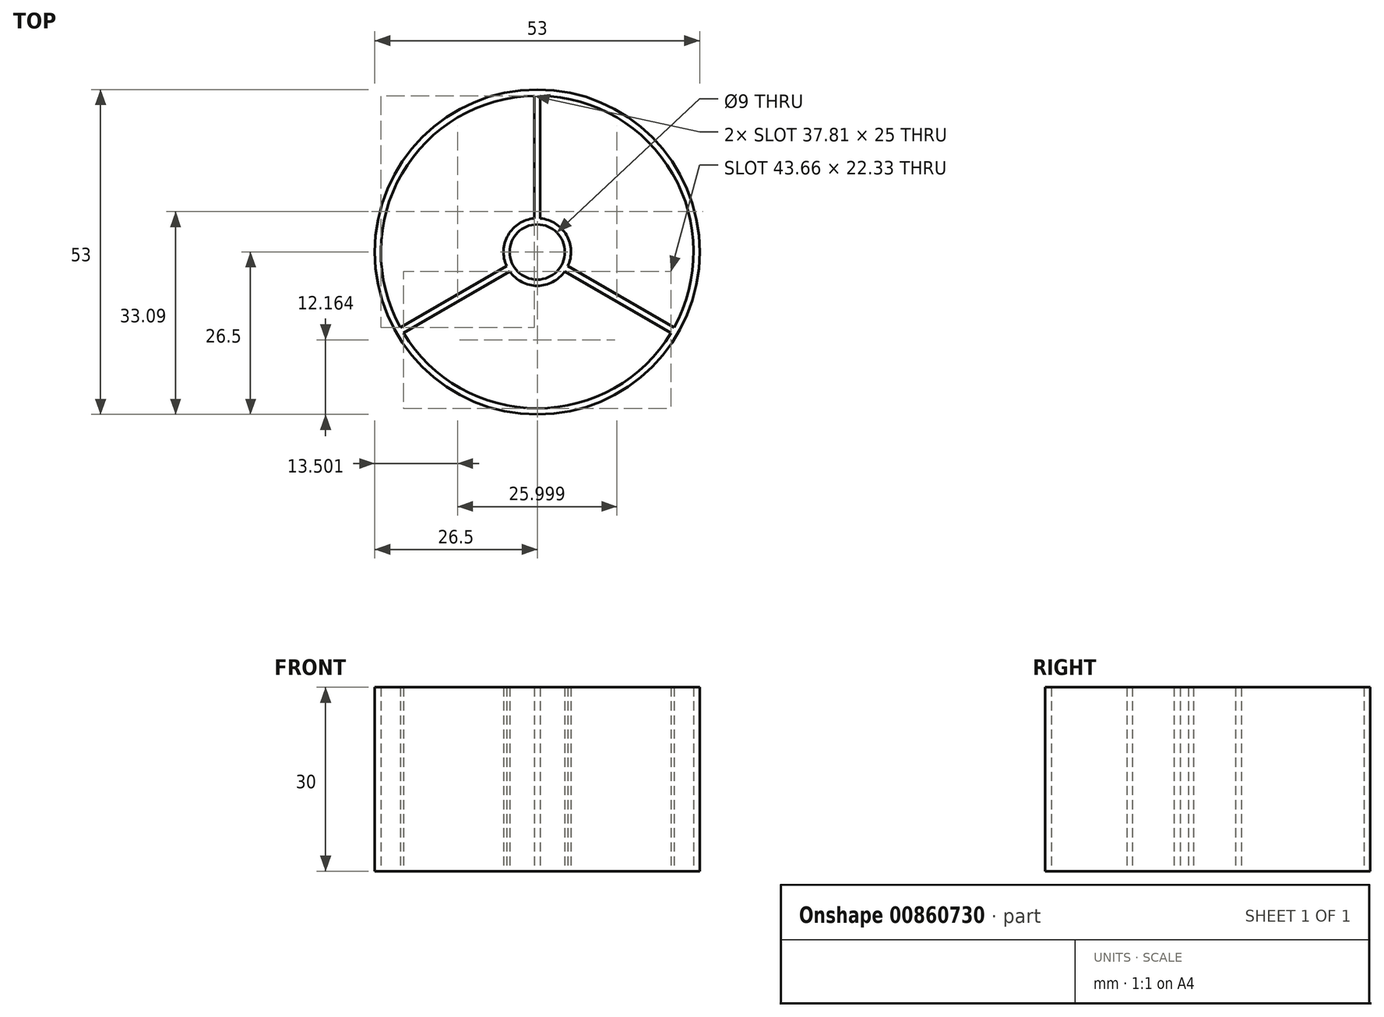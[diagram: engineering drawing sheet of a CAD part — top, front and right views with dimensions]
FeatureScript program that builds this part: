
annotation { "Feature Type Name" : "Feature", "Feature Type Description" : "" }
export const myFeature = defineFeature(function(context is Context, id is Id, definition is map)
    precondition{}
    {
        {
            var Q0;
            Q0=qCreatedBy(makeId("Top.planeOp"),FACE);
            var sketch = newSketch(context, id + "F0", { "sketchPlane" : qUnion([Q0])});
            skCircle(sketch, "E0", {"center": v(0, 0) * mm, "radius": 26.5 * mm});
            skCircle(sketch, "E1.0", {"center": v(0, 0) * mm, "radius": 25.5 * mm});
            skCircle(sketch, "E2", {"center": v(0, 0) * mm, "radius": 4.5 * mm});
            skCircle(sketch, "E3.0", {"center": v(0, 0) * mm, "radius": 5.5 * mm});
            skLineSegment(sketch, "E4", {"start": v(-0.5, 5.48) * mm, "end": v(-0.5, 25.5) * mm});
            skLineSegment(sketch, "E5", {"start": v(0.5, 5.48) * mm, "end": v(0.5, 25.5) * mm});
            skLineSegment(sketch, "E6.1.0", {"start": v(-4.5, -3.17) * mm, "end": v(-21.83, -13.18) * mm});
            skLineSegment(sketch, "E6.1.1", {"start": v(-5, -2.3) * mm, "end": v(-22.33, -12.31) * mm});
            skLineSegment(sketch, "E6.2.0", {"start": v(5, -2.3) * mm, "end": v(22.33, -12.31) * mm});
            skLineSegment(sketch, "E6.2.1", {"start": v(4.5, -3.17) * mm, "end": v(21.83, -13.18) * mm});
            skSolve(sketch);
        }
        {
            var Q0;
            Q0=makeQuery(id+"F0.imprint","IMPRINT",FACE,{"disambiguationData":[TD([[makeQuery(id+"F0.imprint","IMPRINT",EDGE,{"derivedFrom":sQuery(id+"F0.wireOp",EDGE,"E0")}),1.0]])]});
            var Q1;
            Q1=makeQuery(id+"F0.imprint","IMPRINT",FACE,{"disambiguationData":[TD([[makeQuery(id+"F0.imprint","IMPRINT",EDGE,{"derivedFrom":sQuery(id+"F0.wireOp",EDGE,"E2")}),-1.0]])]});
            var Q2;
            {var subQ0=sQuery(id+"F0.wireOp",EDGE,"E4");Q2=makeQuery(id+"F0.imprint","IMPRINT",FACE,{"disambiguationData":[TD([[makeQuery(id+"F0.imprint","IMPRINT",EDGE,{"derivedFrom":subQ0}),-1.0]])]});}
            var Q3;
            {var subQ0=sQuery(id+"F0.wireOp",EDGE,"E6.1.0");Q3=makeQuery(id+"F0.imprint","IMPRINT",FACE,{"disambiguationData":[TD([[makeQuery(id+"F0.imprint","IMPRINT",EDGE,{"derivedFrom":subQ0}),-1.0]])]});}
            var Q4;
            {var subQ0=sQuery(id+"F0.wireOp",EDGE,"E6.2.0");Q4=makeQuery(id+"F0.imprint","IMPRINT",FACE,{"disambiguationData":[TD([[makeQuery(id+"F0.imprint","IMPRINT",EDGE,{"derivedFrom":subQ0}),-1.0]])]});}
            extrude(context, id + "F1", {"entities" : qUnion([Q0, Q1, Q2, Q3, Q4]), "depth" : 30 * mm, "offsetDistance" : 25 * mm});
        }
    });
